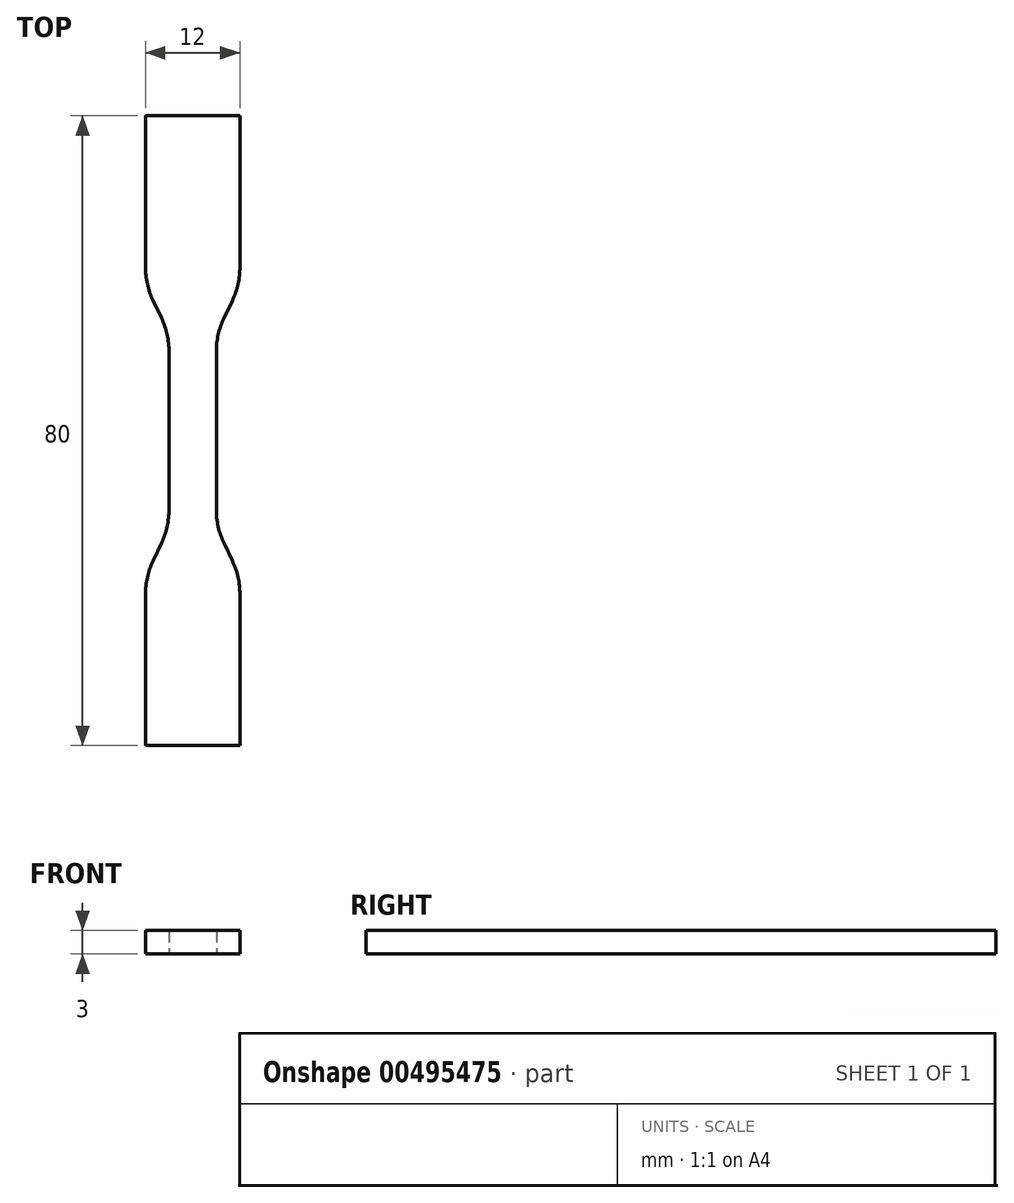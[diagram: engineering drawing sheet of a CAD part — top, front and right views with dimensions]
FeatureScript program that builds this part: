
annotation { "Feature Type Name" : "Feature", "Feature Type Description" : "" }
export const myFeature = defineFeature(function(context is Context, id is Id, definition is map)
    precondition{}
    {
        {
            var Q0;
            Q0=qCreatedBy(makeId("Top.planeOp"),FACE);
            var sketch = newSketch(context, id + "F0", { "sketchPlane" : qUnion([Q0])});
            skLineSegment(sketch, "E0", {"start": v(0, 0) * mm, "end": v(3, 0) * mm, "construction": true});
            skLineSegment(sketch, "E1", {"start": v(3, 0) * mm, "end": v(3, 10) * mm});
            skLineSegment(sketch, "E2", {"start": v(3.96, 14.28) * mm, "end": v(5.04, 16.54) * mm});
            skLineSegment(sketch, "E3", {"start": v(6, 20.83) * mm, "end": v(6, 40) * mm});
            skLineSegment(sketch, "E4", {"start": v(6, 40) * mm, "end": v(0, 40) * mm});
            skPoint(sketch, "E5.visualSharp", {"position": v(3, 12.25) * mm});
            skArc(sketch, "E5.filletArc", {"start": v(3.96, 14.28) * mm, "mid": v(3.24, 12.2) * mm, "end": v(3, 10) * mm});
            skPoint(sketch, "E6.visualSharp", {"position": v(6, 18.58) * mm});
            skArc(sketch, "E6.filletArc", {"start": v(5.04, 16.54) * mm, "mid": v(5.76, 18.63) * mm, "end": v(6, 20.83) * mm});
            skLineSegment(sketch, "E7", {"start": v(0, 40) * mm, "end": v(0, 0) * mm, "construction": true});
            skLineSegment(sketch, "E8.MirrorCS", {"start": v(-3, 0) * mm, "end": v(-3, 10) * mm});
            skArc(sketch, "E9.MirrorCS", {"start": v(-3.96, 14.28) * mm, "mid": v(-3.24, 12.2) * mm, "end": v(-3, 10) * mm});
            skLineSegment(sketch, "E10.MirrorCS", {"start": v(-3.96, 14.28) * mm, "end": v(-5.04, 16.54) * mm});
            skArc(sketch, "E11.MirrorCS", {"start": v(-5.04, 16.54) * mm, "mid": v(-5.76, 18.63) * mm, "end": v(-6, 20.83) * mm});
            skLineSegment(sketch, "E12.MirrorCS", {"start": v(-6, 40) * mm, "end": v(0, 40) * mm});
            skLineSegment(sketch, "E13.MirrorCS", {"start": v(-6, 20.83) * mm, "end": v(-6, 40) * mm});
            skLineSegment(sketch, "E14.MirrorCS", {"start": v(3.96, -14.28) * mm, "end": v(5.04, -16.54) * mm});
            skLineSegment(sketch, "E15.MirrorCS", {"start": v(-3.96, -14.28) * mm, "end": v(-5.04, -16.54) * mm});
            skArc(sketch, "E16.MirrorCS", {"start": v(5.04, -16.54) * mm, "mid": v(5.76, -18.63) * mm, "end": v(6, -20.83) * mm});
            skArc(sketch, "E17.MirrorCS", {"start": v(3.96, -14.28) * mm, "mid": v(3.24, -12.2) * mm, "end": v(3, -10) * mm});
            skLineSegment(sketch, "E18.MirrorCS", {"start": v(0, -40) * mm, "end": v(0, 0) * mm, "construction": true});
            skPoint(sketch, "E19.MirrorP", {"position": v(6, -18.58) * mm});
            skLineSegment(sketch, "E20.MirrorCS", {"start": v(3, 0) * mm, "end": v(3, -10) * mm});
            skLineSegment(sketch, "E21.MirrorCS", {"start": v(6, -20.83) * mm, "end": v(6, -40) * mm});
            skLineSegment(sketch, "E22.MirrorCS", {"start": v(6, -40) * mm, "end": v(0, -40) * mm});
            skLineSegment(sketch, "E23.MirrorCS", {"start": v(-3, 0) * mm, "end": v(-3, -10) * mm});
            skPoint(sketch, "E24.MirrorP", {"position": v(3, -12.25) * mm});
            skLineSegment(sketch, "E25.MirrorCS", {"start": v(-6, -20.83) * mm, "end": v(-6, -40) * mm});
            skLineSegment(sketch, "E26.MirrorCS", {"start": v(-6, -40) * mm, "end": v(0, -40) * mm});
            skArc(sketch, "E27.MirrorCS", {"start": v(-3.96, -14.28) * mm, "mid": v(-3.24, -12.2) * mm, "end": v(-3, -10) * mm});
            skArc(sketch, "E28.MirrorCS", {"start": v(-5.04, -16.54) * mm, "mid": v(-5.76, -18.63) * mm, "end": v(-6, -20.83) * mm});
            skSolve(sketch);
        }
        {
            var Q0;
            Q0=makeQuery(id+"F0.imprint","IMPRINT",FACE,{"disambiguationData":[TD([[makeQuery(id+"F0.imprint","IMPRINT",EDGE,{"derivedFrom":sQuery(id+"F0.wireOp",EDGE,"E1")}),1.0]])]});
            extrude(context, id + "F1", {"entities" : qUnion([Q0]), "depth" : 3 * mm});
        }
    });
